FCSTD DOCUMENT  (FreeCAD 0.19R)
Label: ugly-vase-generator
License: All rights reserved
LicenseURL: http://en.wikipedia.org/wiki/All_rights_reserved
objects: Sketcher::SketchObject×1
note: 1 computed .brp shape members not serialized (recipe doc carries the construction recipe); baked Part::Feature solids carry a one-line shape summary decoded from their .brp

FEATURE [Sketcher::SketchObject] Sketch
  MapMode = 5
  sketch-geometry (7):
    g0: LineSegment StartX=17.7535 StartY=10.25 StartZ=0 EndX=2.451e-13 EndY=20.5 EndZ=0
    g1: LineSegment StartX=2.451e-13 StartY=20.5 StartZ=0 EndX=-17.7535 EndY=10.25 EndZ=0
    g2: LineSegment StartX=-17.7535 StartY=10.25 StartZ=0 EndX=-17.7535 EndY=-10.25 EndZ=0
    g3: LineSegment StartX=-17.7535 StartY=-10.25 StartZ=0 EndX=3.6e-15 EndY=-20.5 EndZ=0
    g4: LineSegment StartX=3.6e-15 StartY=-20.5 StartZ=0 EndX=17.7535 EndY=-10.25 EndZ=0
    g5: LineSegment StartX=17.7535 StartY=-10.25 StartZ=0 EndX=17.7535 EndY=10.25 EndZ=0
    g6: Circle [constr] CenterX=0 CenterY=0 CenterZ=0 NormalX=0 NormalY=0 NormalZ=1 AngleXU=0 Radius=20.5
  constraints (16):
    c: Coincident(g0,g1)
    c: Coincident(g1,g2)
    c: Coincident(g2,g3)
    c: Coincident(g3,g4)
    c: Coincident(g4,g5)
    c: Coincident(g5,g0)
    c: Equal(g0, g1-g5) x5
    c: PointOnObject(g0,g6)
    c: PointOnObject(g1,g6)
    c: PointOnObject(g2,g6)
    c: PointOnObject(g3,g6)
    c: PointOnObject(g4,g6)
    c: PointOnObject(g5,g6)
    c: Coincident(g6,g-1)
    c: Diameter(g6) = 41  'diameter'
    c: Angle(g-2,g5) = 0  'angle'
